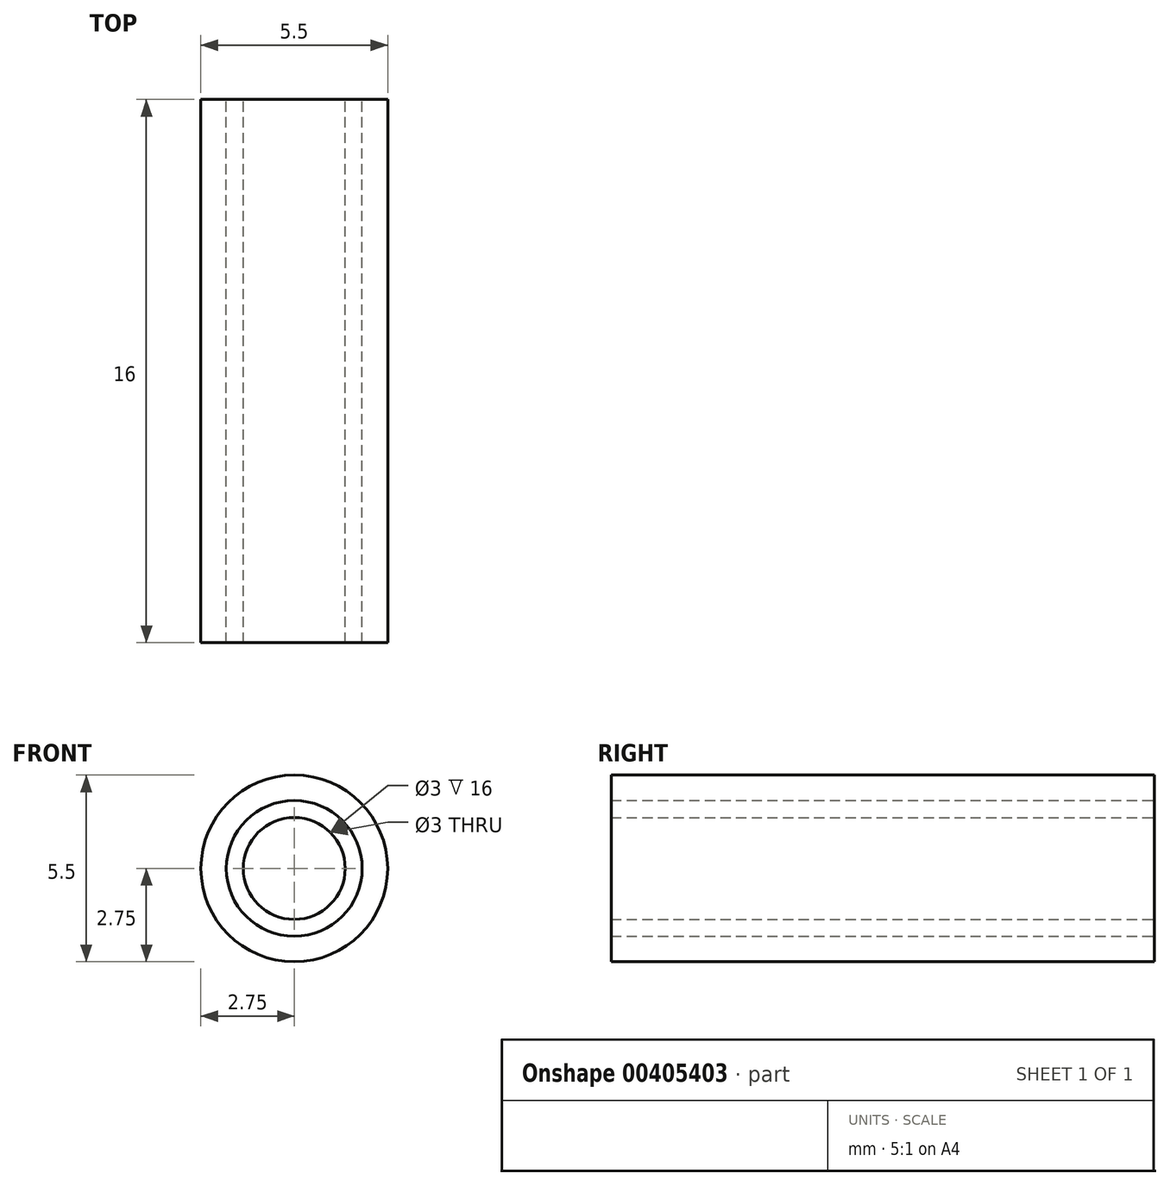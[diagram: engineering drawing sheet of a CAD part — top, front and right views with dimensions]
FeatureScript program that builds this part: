
annotation { "Feature Type Name" : "Feature", "Feature Type Description" : "" }
export const myFeature = defineFeature(function(context is Context, id is Id, definition is map)
    precondition{}
    {
        {
            var Q0;
            Q0=qCreatedBy(makeId("Front.planeOp"),FACE);
            var sketch = newSketch(context, id + "F0", { "sketchPlane" : qUnion([Q0])});
            skCircle(sketch, "E0", {"center": v(0, 0) * mm, "radius": 2.75 * mm});
            skCircle(sketch, "E1", {"center": v(0, 0) * mm, "radius": 1.5 * mm});
            skSolve(sketch);
        }
        {
            var Q0;
            Q0=qSketchRegion(id+"F0",true);
            extrude(context, id + "F1", {"entities" : qUnion([Q0]), "depth" : 16 * mm});
        }
        {
            var Q0;
            Q0=qCreatedBy(makeId("Front.planeOp"),FACE);
            var sketch = newSketch(context, id + "F2", { "sketchPlane" : qUnion([Q0])});
            skCircle(sketch, "E2", {"center": v(0, 0) * mm, "radius": 1.5 * mm});
            skCircle(sketch, "E3", {"center": v(0, 0) * mm, "radius": 2 * mm});
            skSolve(sketch);
        }
        {
            var Q0;
            Q0=qSketchRegion(id+"F2",true);
            extrude(context, id + "F3", {"entities" : qUnion([Q0]), "depth" : 16 * mm});
        }
    });
